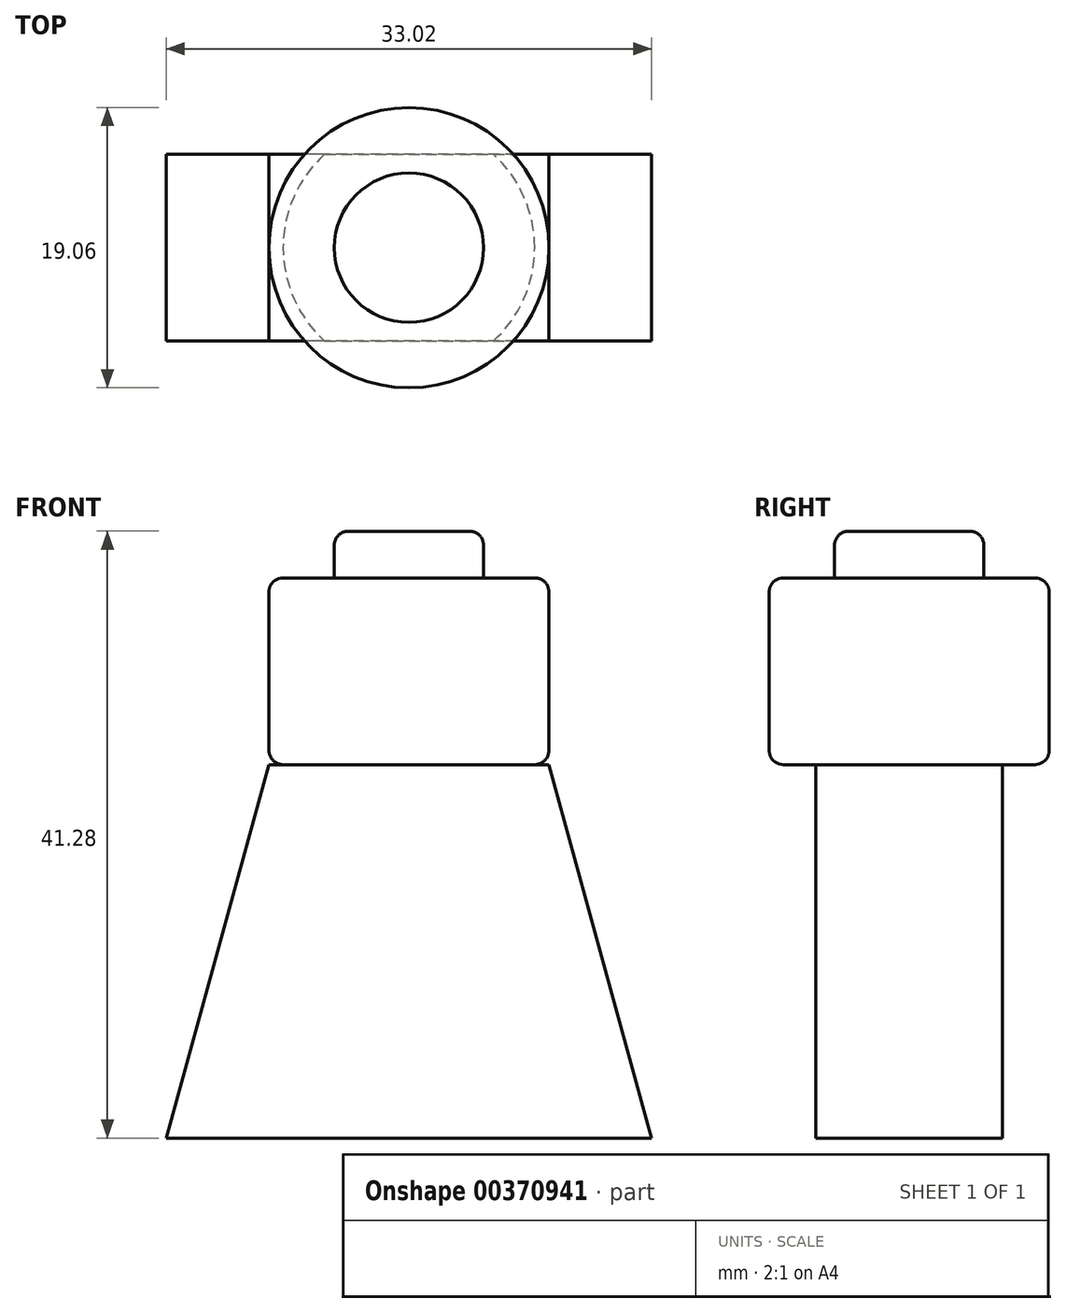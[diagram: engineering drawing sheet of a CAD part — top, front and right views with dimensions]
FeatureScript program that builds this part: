
annotation { "Feature Type Name" : "Feature", "Feature Type Description" : "" }
export const myFeature = defineFeature(function(context is Context, id is Id, definition is map)
    precondition{}
    {
        {
            var Q0;
            Q0=qCreatedBy(makeId("Front.planeOp"),FACE);
            var sketch = newSketch(context, id + "F0", { "sketchPlane" : qUnion([Q0])});
            skLineSegment(sketch, "E0.top", {"start": v(0, 0) * mm, "end": v(8.56, 0) * mm});
            skLineSegment(sketch, "E0.right", {"start": v(9.53, 11.74) * mm, "end": v(9.53, 0.97) * mm});
            skLineSegment(sketch, "E1.top", {"start": v(4.12, 15.88) * mm, "end": v(0, 15.88) * mm});
            skLineSegment(sketch, "E1.left", {"start": v(5.08, 12.7) * mm, "end": v(5.08, 14.92) * mm});
            skLineSegment(sketch, "E2.trimOffspring", {"start": v(5.08, 12.7) * mm, "end": v(8.57, 12.7) * mm});
            skLineSegment(sketch, "E3", {"start": v(0, 15.88) * mm, "end": v(0, 0) * mm});
            skPoint(sketch, "E1.right.end.orphan", {"position": v(-5.08, 15.88) * mm});
            skPoint(sketch, "E4.visualSharp", {"position": v(5.08, 15.88) * mm});
            skArc(sketch, "E4.filletArc", {"start": v(5.08, 14.92) * mm, "mid": v(4.8, 15.6) * mm, "end": v(4.12, 15.88) * mm});
            skPoint(sketch, "E5.visualSharp", {"position": v(9.53, 12.7) * mm});
            skArc(sketch, "E5.filletArc", {"start": v(9.53, 11.74) * mm, "mid": v(9.24, 12.42) * mm, "end": v(8.57, 12.7) * mm});
            skPoint(sketch, "E6.visualSharp", {"position": v(9.53, 0) * mm});
            skArc(sketch, "E6.filletArc", {"start": v(8.56, 0) * mm, "mid": v(9.24, 0.28) * mm, "end": v(9.53, 0.97) * mm});
            skSolve(sketch);
        }
        {
            var Q0;
            Q0=makeQuery(id+"F0.imprint","IMPRINT",FACE,{"disambiguationData":[TD([[makeQuery(id+"F0.imprint","IMPRINT",EDGE,{"derivedFrom":sQuery(id+"F0.wireOp",EDGE,"E0.top")}),1.0]])]});
            var Q1;
            Q1=sQuery(id+"F0.wireOp",EDGE,"E3");
            revolve(context, id + "F1", {"entities" : qUnion([Q0]), "axis" : qUnion([Q1]), "revolveType" : RevolveType.FULL});
        }
        {
            var Q0;
            Q0=qCreatedBy(makeId("Front.planeOp"),FACE);
            var sketch = newSketch(context, id + "F2", { "sketchPlane" : qUnion([Q0])});
            skLineSegment(sketch, "E7", {"start": v(0, 0) * mm, "end": v(9.53, 0) * mm});
            skLineSegment(sketch, "E8", {"start": v(9.53, 0) * mm, "end": v(16.51, -25.4) * mm});
            skLineSegment(sketch, "E9", {"start": v(16.51, -25.4) * mm, "end": v(0, -25.4) * mm});
            skLineSegment(sketch, "E10", {"start": v(0, -25.4) * mm, "end": v(0, 0) * mm});
            skSolve(sketch);
        }
        {
            var Q0;
            Q0=makeQuery(id+"F2.imprint","IMPRINT",FACE,{"disambiguationData":[TD([[makeQuery(id+"F2.imprint","IMPRINT",EDGE,{"derivedFrom":sQuery(id+"F2.wireOp",EDGE,"E7")}),-1.0]])]});
            extrude(context, id + "F3", {"entities" : qUnion([Q0]), "operationType" : NewBodyOperationType.ADD, "endBound" : BoundingType.SYMMETRIC, "depth" : 12.7 * mm});
        }
        {
            var Q0;
            Q0=makeQuery(id+"F1.opRevolve","SWEPT_BODY",BODY,{"disambiguationData":[OSD([sQuery(id+"F0.wireOp",EDGE,"E0.top"),sQuery(id+"F0.wireOp",EDGE,"E0.right"),sQuery(id+"F0.wireOp",EDGE,"E1.top"),sQuery(id+"F0.wireOp",EDGE,"E1.left"),sQuery(id+"F0.wireOp",EDGE,"E2.trimOffspring"),sQuery(id+"F0.wireOp",EDGE,"E3"),sQuery(id+"F0.wireOp",EDGE,"E4.filletArc"),sQuery(id+"F0.wireOp",EDGE,"E5.filletArc"),sQuery(id+"F0.wireOp",EDGE,"E6.filletArc")])]});
            var Q1;
            Q1=qCreatedBy(makeId("Right.planeOp"),FACE);
            mirror(context, id + "F4", {"operationType" : NewBodyOperationType.ADD, "entities" : qUnion([Q0]), "mirrorPlane" : qUnion([Q1])});
        }
    });
